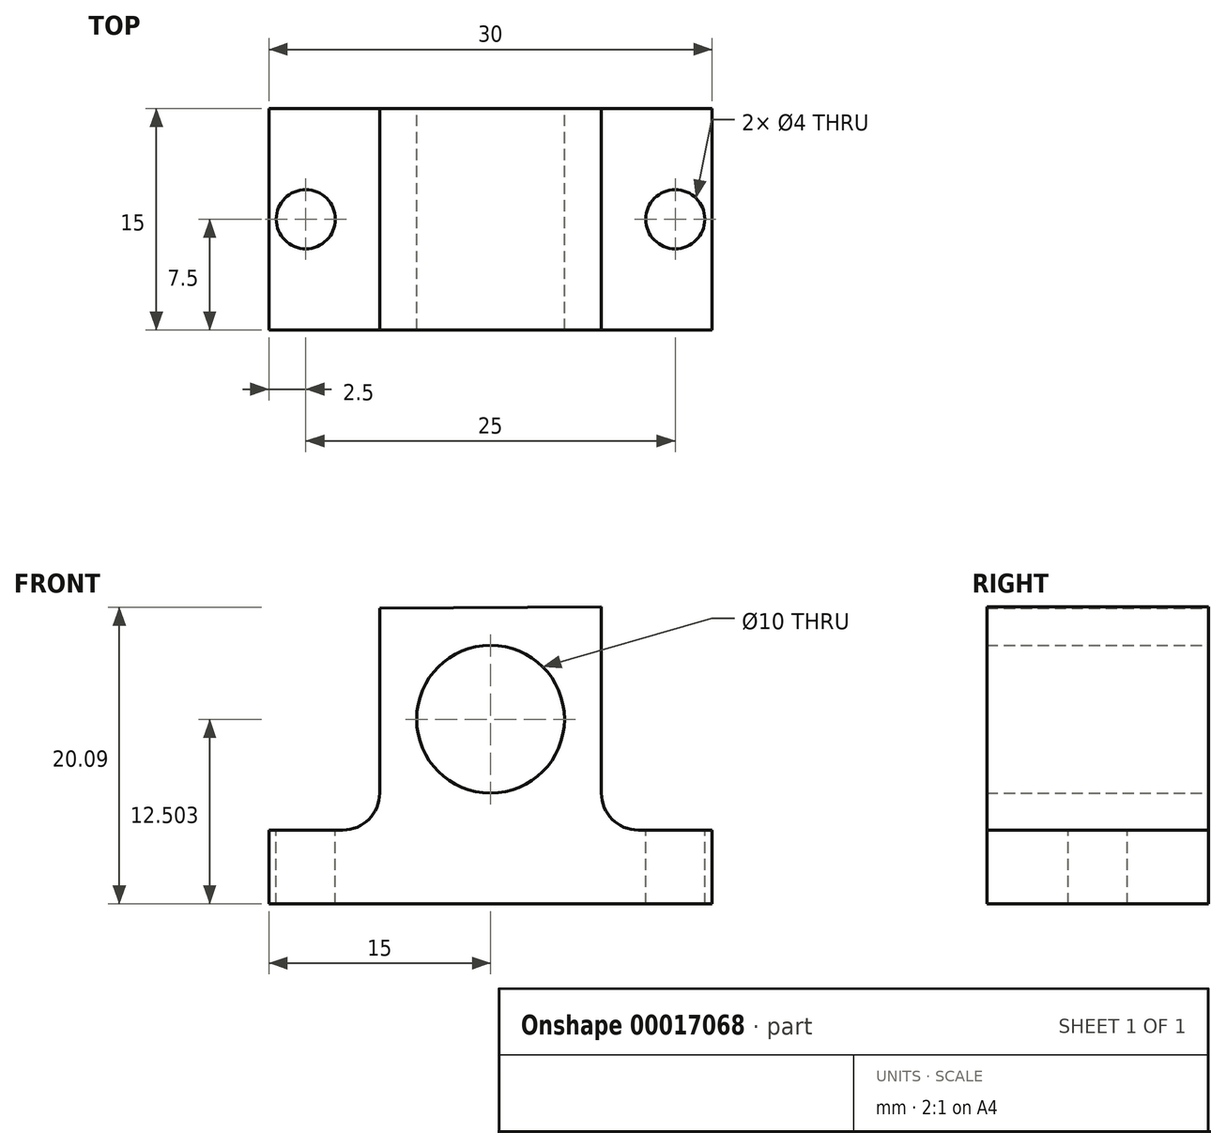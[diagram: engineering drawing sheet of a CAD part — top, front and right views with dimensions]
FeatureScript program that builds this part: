
annotation { "Feature Type Name" : "Feature", "Feature Type Description" : "" }
export const myFeature = defineFeature(function(context is Context, id is Id, definition is map)
    precondition{}
    {
        {
            var Q0;
            Q0=qCreatedBy(makeId("Front.planeOp"),FACE);
            var sketch = newSketch(context, id + "F0", { "sketchPlane" : qUnion([Q0])});
            skLineSegment(sketch, "E0", {"start": v(-22.5, 19.31) * mm, "end": v(-22.5, 6.81) * mm});
            skLineSegment(sketch, "E1", {"start": v(-7.5, 6.81) * mm, "end": v(-7.5, 19.4) * mm});
            skLineSegment(sketch, "E2", {"start": v(-7.5, 19.4) * mm, "end": v(-22.5, 19.31) * mm});
            skLineSegment(sketch, "E3", {"start": v(-25, 4.31) * mm, "end": v(-30, 4.31) * mm});
            skLineSegment(sketch, "E4", {"start": v(-30, -0.69) * mm, "end": v(0, -0.69) * mm});
            skLineSegment(sketch, "E5", {"start": v(0, -0.69) * mm, "end": v(0, 4.31) * mm});
            skLineSegment(sketch, "E6", {"start": v(0, 4.31) * mm, "end": v(-5, 4.31) * mm});
            skLineSegment(sketch, "E7", {"start": v(-30, -0.69) * mm, "end": v(-30, 4.31) * mm});
            skPoint(sketch, "E8.visualSharp", {"position": v(-22.5, 4.31) * mm});
            skArc(sketch, "E8.filletArc", {"start": v(-25, 4.31) * mm, "mid": v(-23.23, 5.05) * mm, "end": v(-22.5, 6.81) * mm});
            skPoint(sketch, "E9.visualSharp", {"position": v(-7.5, 4.31) * mm});
            skArc(sketch, "E9.filletArc", {"start": v(-7.5, 6.81) * mm, "mid": v(-6.77, 5.05) * mm, "end": v(-5, 4.31) * mm});
            skCircle(sketch, "E10", {"center": v(-15, 11.81) * mm, "radius": 5 * mm});
            skSolve(sketch);
        }
        {
            var Q0;
            Q0 = qSketchRegion(id + "F0", true);
            extrude(context, id + "F1", {"entities" : qUnion([Q0]), "depth" : 15 * mm});
        }
        {
            var Q0;
            Q0=makeQuery(id+"F1.opExtrude","SWEPT_FACE",FACE,{"disambiguationData":[OSD([sQuery(id+"F0.wireOp",EDGE,"E3")])]});
            var sketch = newSketch(context, id + "F2", { "sketchPlane" : qUnion([Q0])});
            skCircle(sketch, "E11", {"center": v(-27.5, -7.5) * mm, "radius": 2 * mm});
            skLineSegment(sketch, "E12", {"start": v(-27.5, -15) * mm, "end": v(-30, -15) * mm});
            skLineSegment(sketch, "E13", {"start": v(-30, -15) * mm, "end": v(-27.5, -15) * mm});
            skSolve(sketch);
        }
        {
            var Q0;
            Q0=makeQuery(id+"F1.opExtrude","SWEPT_FACE",FACE,{"disambiguationData":[OSD([sQuery(id+"F0.wireOp",EDGE,"E6")])]});
            var sketch = newSketch(context, id + "F3", { "sketchPlane" : qUnion([Q0])});
            skCircle(sketch, "E14", {"center": v(-2.5, -7.5) * mm, "radius": 2 * mm});
            skSolve(sketch);
        }
        {
            var Q0;
            Q0=makeQuery(id+"F2.imprint","IMPRINT",FACE,{"disambiguationData":[TD([[makeQuery(id+"F2.imprint","IMPRINT",EDGE,{"derivedFrom":sQuery(id+"F2.wireOp",EDGE,"E11")}),1.0]])]});
            var sketch = newSketch(context, id + "F4", { "sketchPlane" : qUnion([Q0])});
            skSolve(sketch);
        }
        {
            var Q0;
            Q0 = qSketchRegion(id + "F4", true);
            var Q1;
            Q1=makeQuery(id+"F2.imprint","IMPRINT",FACE,{"disambiguationData":[TD([[makeQuery(id+"F2.imprint","IMPRINT",EDGE,{"derivedFrom":sQuery(id+"F2.wireOp",EDGE,"E11")}),1.0]])]});
            extrude(context, id + "F5", {"entities" : qUnion([Q0, Q1]), "operationType" : NewBodyOperationType.REMOVE, "endBound" : BoundingType.THROUGH_ALL, "oppositeDirection" : true, "depth" : 25 * mm});
        }
        {
            var Q0;
            Q0=makeQuery(id+"F3.imprint","IMPRINT",FACE,{"disambiguationData":[TD([[makeQuery(id+"F3.imprint","IMPRINT",EDGE,{"derivedFrom":sQuery(id+"F3.wireOp",EDGE,"E14")}),1.0]])]});
            extrude(context, id + "F6", {"entities" : qUnion([Q0]), "operationType" : NewBodyOperationType.REMOVE, "endBound" : BoundingType.THROUGH_ALL, "oppositeDirection" : true, "depth" : 25 * mm});
        }
    });
